# Revit family: Access_Door-Fire_Rated-Cendrex-Uninsulated-Plaster_Flange-Walls_Only-(PFN-PLY)
name_source: partatom
category: Specialty Equipment
revit_build: Autodesk Revit Architecture 2013 (Build: 20130531_2115(x64)
units: mm (PartAtom-declared; Revit-internal decimal feet)

## types (15) — shared parameters
Assembly Code = C1020700
Available Options = http://cendrex.com
Cendrex LEED Ready Program = http://www.cendrex.com
Construction Material = Metal - Cendrex - Aluminum
Default Elevation = 0"
Description = Fire rated uninsulated access door with plaster flange for walls only
Door Height = 24"
Door Width = 24"
Finish = Metal - Cendrex - Powder Coated White
Frame Depth = 2 15/32"
Height Actual = 29"
Height Calc = 24"
Manufacturer = Cendrex
Model = PFN-PLY
Product Documentation Link = http://cendrex.com
Product Page URL = http://cendrex.com
URL = http://www.cendrex.com
Width Actual = 29"
Width Calc = 24"

## type names (no varying parameters)
- 8 x 8
- 10 x 10
- 12 x 12
- 14 x 14
- 16 x 16
- 18 x 18
- 22 x 22
- 22 x 30
- 22 x 36
- 24 x 24
- 24 x 36
- 32 x 32
- 30 x 30
- 36 x 36
- Custom

## geometry (parser evidence)
native form markers: Blend x22, Sweep x12
no freeform markers — native parametric forms only
